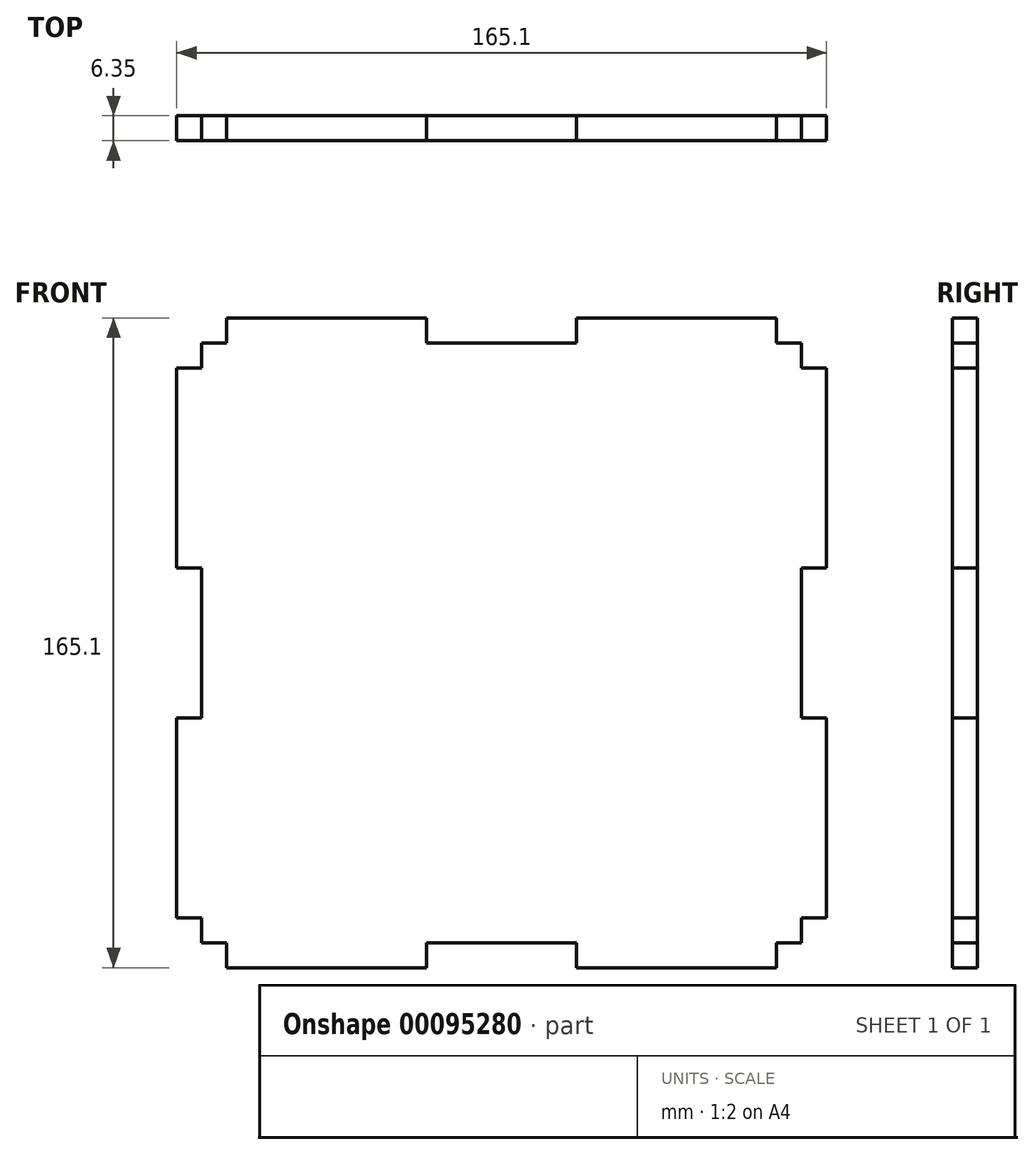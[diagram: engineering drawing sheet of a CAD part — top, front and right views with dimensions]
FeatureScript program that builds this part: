
annotation { "Feature Type Name" : "Feature", "Feature Type Description" : "" }
export const myFeature = defineFeature(function(context is Context, id is Id, definition is map)
    precondition{}
    {
        {
            var Q0;
            Q0=qCreatedBy(makeId("Front.planeOp"),FACE);
            var sketch = newSketch(context, id + "F0", { "sketchPlane" : qUnion([Q0])});
            skLineSegment(sketch, "E0.bottom", {"start": v(76.2, -76.2) * mm, "end": v(-76.2, -76.2) * mm});
            skLineSegment(sketch, "E0.top", {"start": v(76.2, 76.2) * mm, "end": v(-76.2, 76.2) * mm});
            skLineSegment(sketch, "E0.left", {"start": v(76.2, -76.2) * mm, "end": v(76.2, 76.2) * mm});
            skLineSegment(sketch, "E0.right", {"start": v(-76.2, -76.2) * mm, "end": v(-76.2, 76.2) * mm});
            skPoint(sketch, "E0.middle", {"position": v(0, 0) * mm});
            skLineSegment(sketch, "E1.bottom", {"start": v(-69.85, 76.2) * mm, "end": v(-19.05, 76.2) * mm});
            skLineSegment(sketch, "E1.top", {"start": v(-69.85, 82.55) * mm, "end": v(-19.05, 82.55) * mm});
            skLineSegment(sketch, "E1.left", {"start": v(-69.85, 76.2) * mm, "end": v(-69.85, 82.55) * mm});
            skLineSegment(sketch, "E1.right", {"start": v(-19.05, 76.2) * mm, "end": v(-19.05, 82.55) * mm});
            skLineSegment(sketch, "E2", {"start": v(-76.2, 76.2) * mm, "end": v(76.2, -76.2) * mm, "construction": true});
            skLineSegment(sketch, "E3.MirrorCS", {"start": v(-82.55, 69.85) * mm, "end": v(-82.55, 19.05) * mm});
            skLineSegment(sketch, "E4.MirrorCS", {"start": v(-76.2, 69.85) * mm, "end": v(-82.55, 69.85) * mm});
            skLineSegment(sketch, "E5.MirrorCS", {"start": v(-76.2, 19.05) * mm, "end": v(-82.55, 19.05) * mm});
            skLineSegment(sketch, "E6.MirrorCS", {"start": v(76.2, 19.05) * mm, "end": v(82.55, 19.05) * mm});
            skLineSegment(sketch, "E7.MirrorCS", {"start": v(82.55, 69.85) * mm, "end": v(82.55, 19.05) * mm});
            skLineSegment(sketch, "E8.MirrorCS", {"start": v(76.2, 69.85) * mm, "end": v(82.55, 69.85) * mm});
            skLineSegment(sketch, "E9.MirrorCS", {"start": v(69.85, 76.2) * mm, "end": v(69.85, 82.55) * mm});
            skLineSegment(sketch, "E10.MirrorCS", {"start": v(69.85, 82.55) * mm, "end": v(19.05, 82.55) * mm});
            skLineSegment(sketch, "E11.MirrorCS", {"start": v(19.05, 76.2) * mm, "end": v(19.05, 82.55) * mm});
            skLineSegment(sketch, "E12.MirrorCS", {"start": v(19.05, -76.2) * mm, "end": v(19.05, -82.55) * mm});
            skLineSegment(sketch, "E13.MirrorCS", {"start": v(69.85, -82.55) * mm, "end": v(19.05, -82.55) * mm});
            skLineSegment(sketch, "E14.MirrorCS", {"start": v(69.85, -76.2) * mm, "end": v(69.85, -82.55) * mm});
            skLineSegment(sketch, "E15.MirrorCS", {"start": v(76.2, -69.85) * mm, "end": v(82.55, -69.85) * mm});
            skLineSegment(sketch, "E16.MirrorCS", {"start": v(82.55, -69.85) * mm, "end": v(82.55, -19.05) * mm});
            skLineSegment(sketch, "E17.MirrorCS", {"start": v(76.2, -19.05) * mm, "end": v(82.55, -19.05) * mm});
            skLineSegment(sketch, "E18.MirrorCS", {"start": v(-19.05, -76.2) * mm, "end": v(-19.05, -82.55) * mm});
            skLineSegment(sketch, "E19.MirrorCS", {"start": v(-69.85, -82.55) * mm, "end": v(-19.05, -82.55) * mm});
            skLineSegment(sketch, "E20.MirrorCS", {"start": v(-69.85, -76.2) * mm, "end": v(-69.85, -82.55) * mm});
            skLineSegment(sketch, "E21.MirrorCS", {"start": v(-76.2, -69.85) * mm, "end": v(-82.55, -69.85) * mm});
            skLineSegment(sketch, "E22.MirrorCS", {"start": v(-82.55, -69.85) * mm, "end": v(-82.55, -19.05) * mm});
            skLineSegment(sketch, "E23.MirrorCS", {"start": v(-76.2, -19.05) * mm, "end": v(-82.55, -19.05) * mm});
            skSolve(sketch);
        }
        {
            var Q0;
            Q0 = qSketchRegion(id + "F0", true);
            extrude(context, id + "F1", {"entities" : qUnion([Q0]), "depth" : 6.35 * mm});
        }
    });
